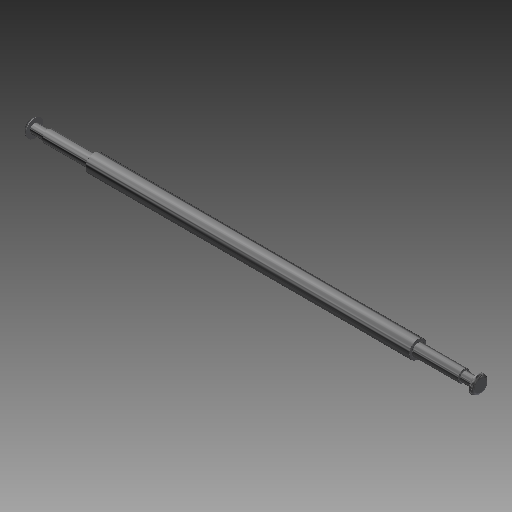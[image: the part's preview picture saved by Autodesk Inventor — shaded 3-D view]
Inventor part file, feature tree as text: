
AUTODESK INVENTOR PART (.ipt)
format: ipt  version: 2019 (Build 230136000, 136)  size: 166,912 bytes
history: native  units: mm
features: plane x2, revolve x1, chamfer x1, fillet x1, split x1, sketch x1, surface_op x1, other x1
ambient origin geometry x8: Origin, YZ Plane, XZ Plane, XY Plane, X Axis, Y Axis, Z Axis, Center Point
bodies: Solid1 (feature_tree)
feature tree (9):
  revolve  "Revolution1"  [1 undecoded]
  chamfer  "Chamfer1"  Distance=10.95mm
  fillet  "Fillet1"  Radius=8.36mm
  split  "Split1"
  plane  "Work Plane1"
  plane  "Work Plane2"
  sketch  "Sketch1"  dims[d0=400.396mm d2=15.84mm d3=10.95mm d4=8.36mm d5=15.84mm d6=10.95mm d7=8.36mm d8=15.84mm d9=289.0mm d10=144.5mm d12=11.6mm d13=11.6mm d15=2.875mm d16=90.0deg d17=0.375mm d18=2.0mm d19=45.0deg d20=0.5mm d21=2.948mm d22=2.948mm d23=-1.745329mm]
  surface_op  "Surface1"
  other  "Srf1"
note: 1 required parameter value undecoded (feature->parameter linkage not recoverable at this tier; creation-order binding heuristic only, values carry confidence <= 0.55)
